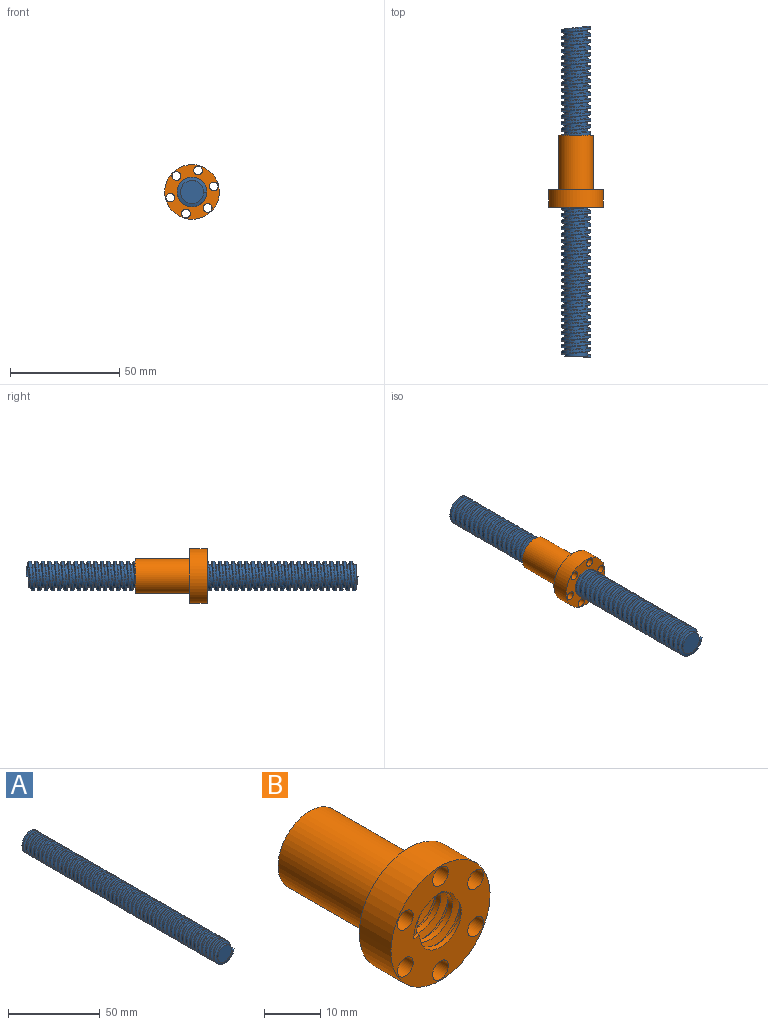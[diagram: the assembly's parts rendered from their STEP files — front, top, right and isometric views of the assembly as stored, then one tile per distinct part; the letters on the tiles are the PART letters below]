
ASSEMBLY  parts=2 mates=1
PART A: 10 faces, bbox 13.5x151.9x15.6 mm
  f0: cylinder r=5.25mm len=150mm, axis (0,-1,0), area 1440.5mm2, adj f1,f2,f4,f5,f7,f9
  f1: plane 10.5x10.5mm, normal (0,1,0), area 86.6mm2, adj f0,f6
  f2: plane 10.5x10.5mm, normal (0,-1,0), area 86.6mm2, adj f0,f3
  f3: cylinder r=5.25mm len=5.25mm, axis (0,-1,0), area 3.1mm2, adj f2,f5,f7
  f4: plane 1.89x1.5mm, normal (0,0,-1), area 2.2mm2, adj f0,f6,f7,f8,f9
  f5: plane 1.89x1.5mm, normal (0,0,1), area 2.2mm2, adj f0,f3,f7,f8,f9
  f6: cylinder r=5.25mm len=9.09mm, axis (0,-1,0), area 7.1mm2, adj f1,f4,f9
  f7: bspline ~150.39x15.59mm, area 2944.5mm2, adj f0,f3,f4,f5,f8
  f8: cylinder r=6.75mm len=151.11mm, axis (0,-1,0), area 2358.2mm2, adj f4,f5,f7,f9
  f9: bspline ~150.39x15.59mm, area 2928.3mm2, adj f0,f4,f5,f6,f8
PART B: 17 faces, bbox 25.4x34.7x25.4 mm
  f0: cylinder r=2mm len=8mm, axis (0,1,0), area 100.5mm2, adj f7,f8
  f1: cylinder r=2mm len=8mm, axis (0,1,0), area 100.5mm2, adj f7,f8
  f2: cylinder r=2mm len=8mm, axis (0,1,0), area 100.5mm2, adj f7,f8
  f3: cylinder r=2mm len=8mm, axis (0,1,0), area 100.5mm2, adj f7,f8
  f4: cylinder r=2mm len=8mm, axis (0,1,0), area 100.5mm2, adj f7,f8
  f5: plane 16.23x16.23mm, normal (0,1,0), area 104.1mm2, adj f9,f10,f11,f14,f15
  f6: cylinder r=12.5mm len=25mm, axis (0,1,0), area 628.3mm2, adj f7,f8
  f7: plane 25.36x25.36mm, normal (0,-1,0), area 311.3mm2, adj f0,f1,f2,f3,f4,f6,f10,f12
  f8: plane 25x25mm, normal (0,1,0), area 214.4mm2, adj f0,f1,f2,f3,f4,f6,f9,f16
  f9: cylinder r=8mm len=25mm, axis (0,-1,0), area 1256.6mm2, adj f5,f8
  f10: cylinder r=5.25mm len=33mm, axis (0,1,0), area 469.5mm2, adj f5,f7,f11,f12,f13,f15
  f11: plane 1.5x1.14mm, normal (0,0,-1), area 1.4mm2, adj f5,f10,f13,f14
  f12: plane 1.5x0.75mm, normal (0,0,1), area 0.8mm2, adj f7,f10,f14,f15
  f13: bspline ~32.89x15.59mm, area 622.5mm2, adj f7,f10,f11,f14
  f14: cylinder r=6.75mm len=33mm, axis (0,-1,0), area 602.3mm2, adj f5,f7,f11,f12,f13,f15
  f15: bspline ~33.39x15.59mm, area 633.2mm2, adj f5,f10,f12,f14
  f16: cylinder r=2mm len=8mm, axis (0,1,0), area 100.5mm2, adj f7,f8
PLACE A at identity fixed
PLACE B rot(axis=(0,-1,0),44.4deg) t=(0,76.25,0)mm
MATE cylindrical A.f0 <-> B.f9  axis (0,-1,0) through (0,75.19,0)mm
